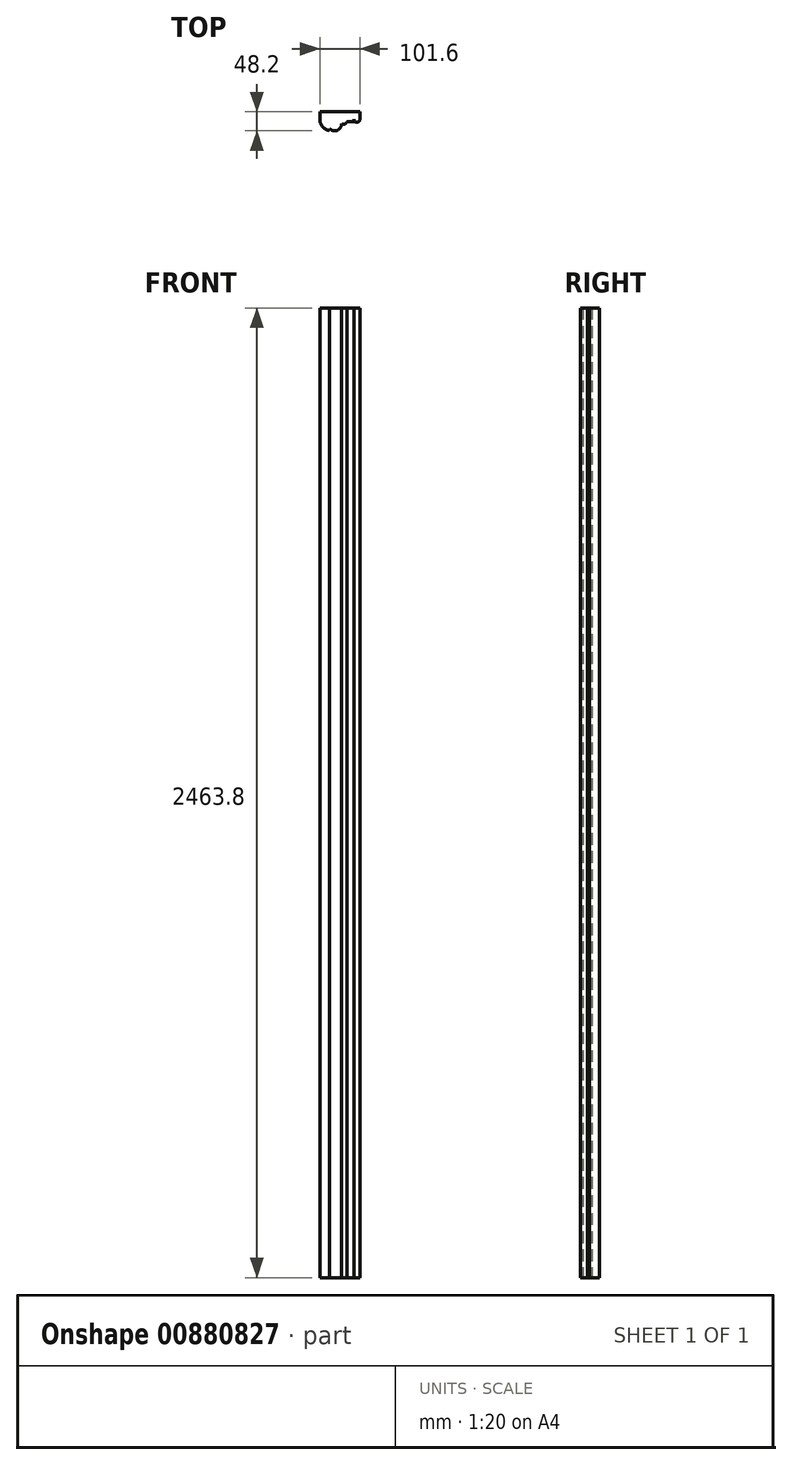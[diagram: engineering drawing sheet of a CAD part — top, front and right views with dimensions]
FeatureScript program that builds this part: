
annotation { "Feature Type Name" : "Feature", "Feature Type Description" : "" }
export const myFeature = defineFeature(function(context is Context, id is Id, definition is map)
    precondition{}
    {
        {
            var Q0;
            Q0=qCreatedBy(makeId("Top.planeOp"),FACE);
            var sketch = newSketch(context, id + "F0", { "sketchPlane" : qUnion([Q0])});
            skLineSegment(sketch, "E0.bottom", {"start": v(0, 0) * mm, "end": v(-101.6, 0) * mm});
            skLineSegment(sketch, "E0.top", {"start": v(0, 25.4) * mm, "end": v(-101.6, 25.4) * mm});
            skLineSegment(sketch, "E0.left", {"start": v(0, 0) * mm, "end": v(0, 25.4) * mm});
            skLineSegment(sketch, "E0.right", {"start": v(-101.6, 0) * mm, "end": v(-101.6, 25.4) * mm});
            skArc(sketch, "E1", {"start": v(-101.6, 0) * mm, "mid": v(-94.46, -18.83) * mm, "end": v(-76.63, -28.2) * mm});
            skLineSegment(sketch, "E2", {"start": v(-76.63, -28.2) * mm, "end": v(-76.63, 0) * mm});
            skArc(sketch, "E3", {"start": v(-76.63, 0) * mm, "mid": v(-63.71, -29.15) * mm, "end": v(-50.8, 0) * mm});
            skArc(sketch, "E4", {"start": v(-50.8, 0) * mm, "mid": v(-41.52, -12.3) * mm, "end": v(-32.23, 0) * mm});
            skArc(sketch, "E5", {"start": v(-15, 0) * mm, "mid": v(-7.5, -7.5) * mm, "end": v(0, 0) * mm});
            skLineSegment(sketch, "E6.bottom", {"start": v(-32.23, 0) * mm, "end": v(-15, 0) * mm});
            skLineSegment(sketch, "E6.top", {"start": v(-32.23, -5.92) * mm, "end": v(-15, -5.92) * mm});
            skLineSegment(sketch, "E6.left", {"start": v(-32.23, 0) * mm, "end": v(-32.23, -5.92) * mm});
            skLineSegment(sketch, "E6.right", {"start": v(-15, 0) * mm, "end": v(-15, -5.92) * mm});
            skLineSegment(sketch, "E7", {"start": v(0, 25.4) * mm, "end": v(0, 19.05) * mm});
            skLineSegment(sketch, "E8", {"start": v(0, 19.05) * mm, "end": v(-101.6, 19.05) * mm});
            skSolve(sketch);
        }
        {
            var Q0;
            {var subQ0=sQuery(id+"F0.wireOp",EDGE,"E1");Q0=makeQuery(id+"F0.imprint","IMPRINT",FACE,{"disambiguationData":[TD([[makeQuery(id+"F0.imprint","IMPRINT",EDGE,{"derivedFrom":subQ0}),1.0]])]});}
            var Q1;
            {var subQ1=sQuery(id+"F0.wireOp",EDGE,"E3");var subQ4=sQuery(id+"F0.wireOp",EDGE,"E2");var subQ6=makeQuery(id+"F0.imprint","INTERSECT",VERTEX,{"derivedFrom":[subQ4,subQ1]});Q1=makeQuery(id+"F0.imprint","IMPRINT",FACE,{"disambiguationData":[TD([[makeQuery(id+"F0.imprint","IMPRINT",EDGE,{"disambiguationData":[TD([[subQ6,-1.0]])],"derivedFrom":subQ1}),1.0]])]});}
            var Q2;
            {var subQ0=sQuery(id+"F0.wireOp",EDGE,"E3");var subQ1=sQuery(id+"F0.wireOp",EDGE,"E2");var subQ2=makeQuery(id+"F0.imprint","INTERSECT",VERTEX,{"derivedFrom":[subQ1,subQ0]});Q2=makeQuery(id+"F0.imprint","IMPRINT",FACE,{"disambiguationData":[TD([[makeQuery(id+"F0.imprint","IMPRINT",EDGE,{"disambiguationData":[TD([[subQ2,-1.0]])],"derivedFrom":subQ1}),1.0]])]});}
            var Q3;
            {var subQ0=sQuery(id+"F0.wireOp",EDGE,"E4");var subQ1=sQuery(id+"F0.wireOp",EDGE,"E3");var subQ3=makeQuery(id+"F0.imprint","INTERSECT",VERTEX,{"derivedFrom":[subQ1,subQ0]});Q3=makeQuery(id+"F0.imprint","IMPRINT",FACE,{"disambiguationData":[TD([[makeQuery(id+"F0.imprint","IMPRINT",EDGE,{"disambiguationData":[TD([[subQ3,-1.0]])],"derivedFrom":subQ1}),1.0]])]});}
            var Q4;
            {var subQ0=sQuery(id+"F0.wireOp",EDGE,"E4");var subQ1=sQuery(id+"F0.wireOp",EDGE,"E3");var subQ6=makeQuery(id+"F0.imprint","INTERSECT",VERTEX,{"derivedFrom":[subQ1,subQ0]});Q4=makeQuery(id+"F0.imprint","IMPRINT",FACE,{"disambiguationData":[TD([[makeQuery(id+"F0.imprint","IMPRINT",EDGE,{"disambiguationData":[TD([[subQ6,-1.0]])],"derivedFrom":subQ0}),1.0]])]});}
            var Q5;
            {var subQ1=sQuery(id+"F0.wireOp",EDGE,"E6.top");Q5=makeQuery(id+"F0.imprint","IMPRINT",FACE,{"disambiguationData":[TD([[makeQuery(id+"F0.imprint","IMPRINT",EDGE,{"derivedFrom":subQ1}),1.0]])]});}
            var Q6;
            {var subQ0=sQuery(id+"F0.wireOp",EDGE,"E6.left");var subQ1=sQuery(id+"F0.wireOp",EDGE,"E4");var subQ3=makeQuery(id+"F0.imprint","INTERSECT",VERTEX,{"derivedFrom":[subQ1,subQ0]});Q6=makeQuery(id+"F0.imprint","IMPRINT",FACE,{"disambiguationData":[TD([[makeQuery(id+"F0.imprint","IMPRINT",EDGE,{"disambiguationData":[TD([[subQ3,-1.0]])],"derivedFrom":subQ1}),1.0]])]});}
            var Q7;
            {var subQ0=sQuery(id+"F0.wireOp",EDGE,"E5");Q7=makeQuery(id+"F0.imprint","IMPRINT",FACE,{"disambiguationData":[TD([[makeQuery(id+"F0.imprint","IMPRINT",EDGE,{"derivedFrom":subQ0}),1.0]])]});}
            var Q8;
            {var subQ7=sQuery(id+"F0.wireOp",EDGE,"E8");Q8=makeQuery(id+"F0.imprint","IMPRINT",FACE,{"disambiguationData":[TD([[makeQuery(id+"F0.imprint","IMPRINT",EDGE,{"derivedFrom":subQ7}),1.0]])]});}
            extrude(context, id + "F1", {"entities" : qUnion([Q0, Q1, Q2, Q3, Q4, Q5, Q6, Q7, Q8]), "depth" : 2463.8 * mm, "offsetDistance" : 25.4 * mm});
        }
    });
